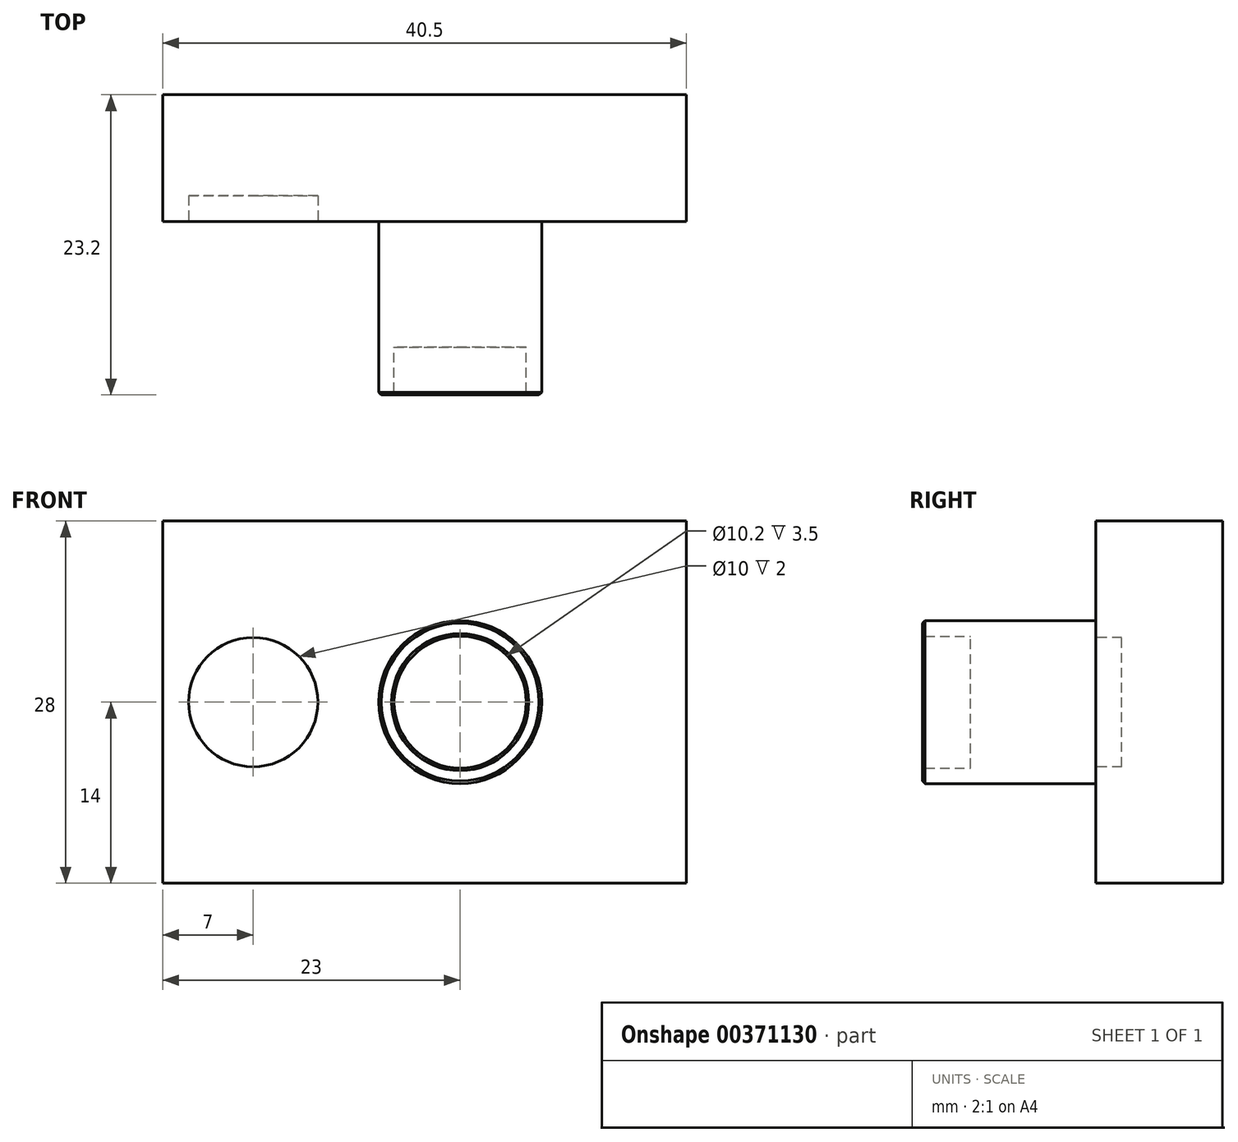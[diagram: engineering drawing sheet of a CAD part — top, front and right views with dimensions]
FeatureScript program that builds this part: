
annotation { "Feature Type Name" : "Feature", "Feature Type Description" : "" }
export const myFeature = defineFeature(function(context is Context, id is Id, definition is map)
    precondition{}
    {
        {
            var Q0;
            Q0=qCreatedBy(makeId("Front.planeOp"),FACE);
            var sketch = newSketch(context, id + "F0", { "sketchPlane" : qUnion([Q0])});
            skLineSegment(sketch, "E0.bottom", {"start": v(0, 0) * mm, "end": v(40.5, 0) * mm});
            skLineSegment(sketch, "E0.top", {"start": v(0, -28) * mm, "end": v(40.5, -28) * mm});
            skLineSegment(sketch, "E0.left", {"start": v(0, 0) * mm, "end": v(0, -28) * mm});
            skLineSegment(sketch, "E0.right", {"start": v(40.5, 0) * mm, "end": v(40.5, -28) * mm});
            skSolve(sketch);
        }
        {
            var Q0;
            Q0=qSketchRegion(id+"F0",true);
            extrude(context, id + "F1", {"entities" : qUnion([Q0]), "depth" : 9.8 * mm});
        }
        {
            var Q0;
            Q0=makeQuery(id+"F1.opExtrude","CAP_FACE",FACE,{"disambiguationData":[OSD([sQuery(id+"F0.wireOp",EDGE,"E0.bottom"),sQuery(id+"F0.wireOp",EDGE,"E0.top"),sQuery(id+"F0.wireOp",EDGE,"E0.left"),sQuery(id+"F0.wireOp",EDGE,"E0.right")])],"isStart":false});
            var sketch = newSketch(context, id + "F2", { "sketchPlane" : qUnion([Q0])});
            skCircle(sketch, "E1", {"center": v(23, -14) * mm, "radius": 6.3 * mm});
            skCircle(sketch, "E2", {"center": v(23, -14) * mm, "radius": 5.1 * mm});
            skLineSegment(sketch, "E3", {"start": v(23, -14) * mm, "end": v(23, 0) * mm, "construction": true});
            skLineSegment(sketch, "E4", {"start": v(23, -14) * mm, "end": v(23, -28) * mm, "construction": true});
            skLineSegment(sketch, "E5", {"start": v(23, -14) * mm, "end": v(40.5, -14) * mm, "construction": true});
            skLineSegment(sketch, "E6", {"start": v(29.3, -14) * mm, "end": v(40.5, -14) * mm, "construction": true});
            skSolve(sketch);
        }
        {
            var Q0;
            Q0=makeQuery(id+"F2.imprint","IMPRINT",FACE,{"disambiguationData":[TD([[makeQuery(id+"F2.imprint","IMPRINT",EDGE,{"derivedFrom":sQuery(id+"F2.wireOp",EDGE,"E1")}),1.0]])]});
            extrude(context, id + "F3", {"entities" : qUnion([Q0]), "operationType" : NewBodyOperationType.ADD, "depth" : 13.4 * mm});
        }
        {
            var Q0;
            Q0=makeQuery(id+"F3.boolean.opBoolean","SPLIT",FACE,{"disambiguationData":[TD([makeQuery(id+"F3.opExtrude","SWEPT_FACE",FACE,{"disambiguationData":[OSD([sQuery(id+"F2.wireOp",EDGE,"E2")])]})])],"derivedFrom":makeQuery(id+"F1.opExtrude","CAP_FACE",FACE,{"disambiguationData":[OSD([sQuery(id+"F0.wireOp",EDGE,"E0.bottom"),sQuery(id+"F0.wireOp",EDGE,"E0.top"),sQuery(id+"F0.wireOp",EDGE,"E0.left"),sQuery(id+"F0.wireOp",EDGE,"E0.right")])],"isStart":false})});
            extrude(context, id + "F4", {"entities" : qUnion([Q0]), "operationType" : NewBodyOperationType.ADD, "depth" : 9.7 * mm});
        }
        {
            var Q0;
            {var subQ0=sQuery(id+"F0.wireOp",EDGE,"E0.left");var subQ1=sQuery(id+"F0.wireOp",EDGE,"E0.top");var subQ2=sQuery(id+"F0.wireOp",EDGE,"E0.right");var subQ3=sQuery(id+"F0.wireOp",EDGE,"E0.bottom");Q0=makeQuery(id+"F3.boolean.opBoolean","SPLIT",FACE,{"disambiguationData":[TD([makeQuery(id+"F1.opExtrude","SWEPT_FACE",FACE,{"disambiguationData":[OSD([subQ3])]})])],"derivedFrom":makeQuery(id+"F1.opExtrude","CAP_FACE",FACE,{"disambiguationData":[OSD([subQ3,subQ1,subQ0,subQ2])],"isStart":false})});}
            var sketch = newSketch(context, id + "F5", { "sketchPlane" : qUnion([Q0])});
            skCircle(sketch, "E7", {"center": v(7, -14) * mm, "radius": 5 * mm});
            skLineSegment(sketch, "E8", {"start": v(7, -14) * mm, "end": v(7, 0) * mm, "construction": true});
            skLineSegment(sketch, "E9", {"start": v(7, -14) * mm, "end": v(7, -28) * mm, "construction": true});
            skLineSegment(sketch, "E10", {"start": v(7, -14) * mm, "end": v(0, -14) * mm, "construction": true});
            skSolve(sketch);
        }
        {
            var Q0;
            Q0=makeQuery(id+"F5.imprint","IMPRINT",FACE,{"disambiguationData":[TD([[makeQuery(id+"F5.imprint","IMPRINT",EDGE,{"derivedFrom":sQuery(id+"F5.wireOp",EDGE,"E7")}),1.0]])]});
            extrude(context, id + "F6", {"entities" : qUnion([Q0]), "operationType" : NewBodyOperationType.REMOVE, "oppositeDirection" : true, "depth" : 2 * mm});
        }
        {
            var Q0;
            Q0=makeQuery(id+"F3.opExtrude","CAP_EDGE",EDGE,{"disambiguationData":[OSD([sQuery(id+"F2.wireOp",EDGE,"E2")])],"isStart":false});
            var Q1;
            Q1=makeQuery(id+"F3.opExtrude","CAP_EDGE",EDGE,{"disambiguationData":[OSD([sQuery(id+"F2.wireOp",EDGE,"E1")])],"isStart":false});
            chamfer(context, id + "F7", {"entities" : qUnion([Q0, Q1]), "width" : 0.2 * mm, "tangentPropagation" : true});
        }
    });
